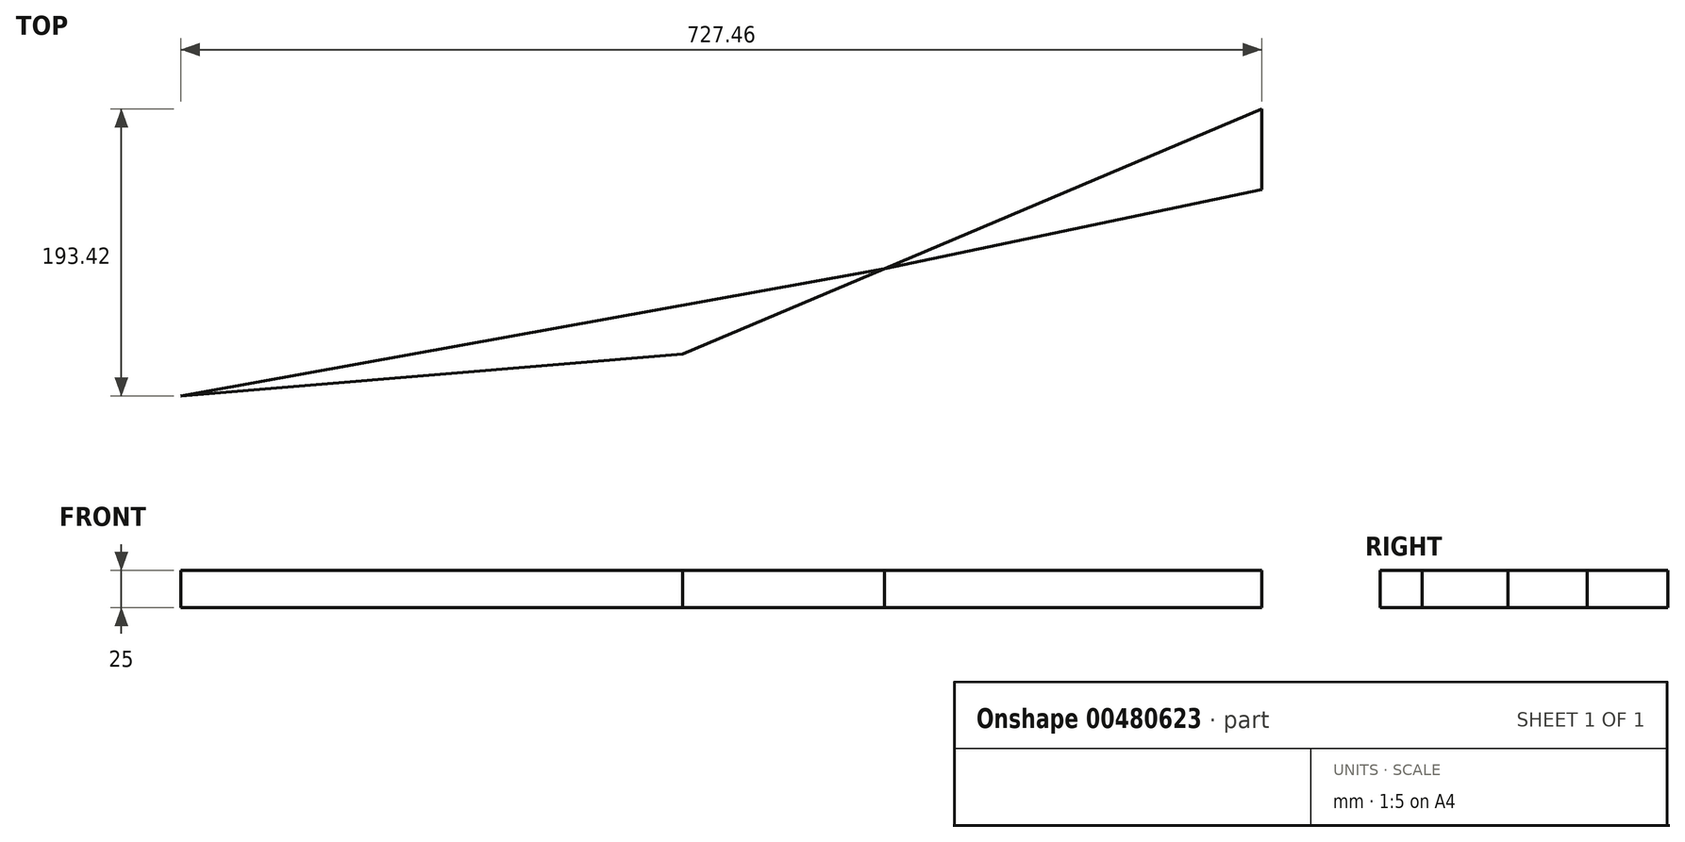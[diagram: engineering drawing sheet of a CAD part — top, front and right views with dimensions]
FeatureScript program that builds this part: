
annotation { "Feature Type Name" : "Feature", "Feature Type Description" : "" }
export const myFeature = defineFeature(function(context is Context, id is Id, definition is map)
    precondition{}
    {
        {
            var Q0;
            Q0=qCreatedBy(makeId("Top.planeOp"),FACE);
            var sketch = newSketch(context, id + "F0", { "sketchPlane" : qUnion([Q0])});
            skLineSegment(sketch, "E0", {"start": v(-135.93, -33.43) * mm, "end": v(253.73, 131.77) * mm});
            skLineSegment(sketch, "E1", {"start": v(253.73, 131.77) * mm, "end": v(253.73, 77.6) * mm});
            skLineSegment(sketch, "E2", {"start": v(253.73, 77.6) * mm, "end": v(0, 24.2) * mm});
            skLineSegment(sketch, "E3", {"start": v(0, 24.2) * mm, "end": v(-473.73, -61.65) * mm});
            skLineSegment(sketch, "E4", {"start": v(-473.73, -61.65) * mm, "end": v(-135.93, -33.43) * mm});
            skSolve(sketch);
        }
        {
            var Q0;
            Q0 = qSketchRegion(id + "F0", true);
            extrude(context, id + "F1", {"entities" : qUnion([Q0]), "depth" : 25 * mm});
        }
    });
